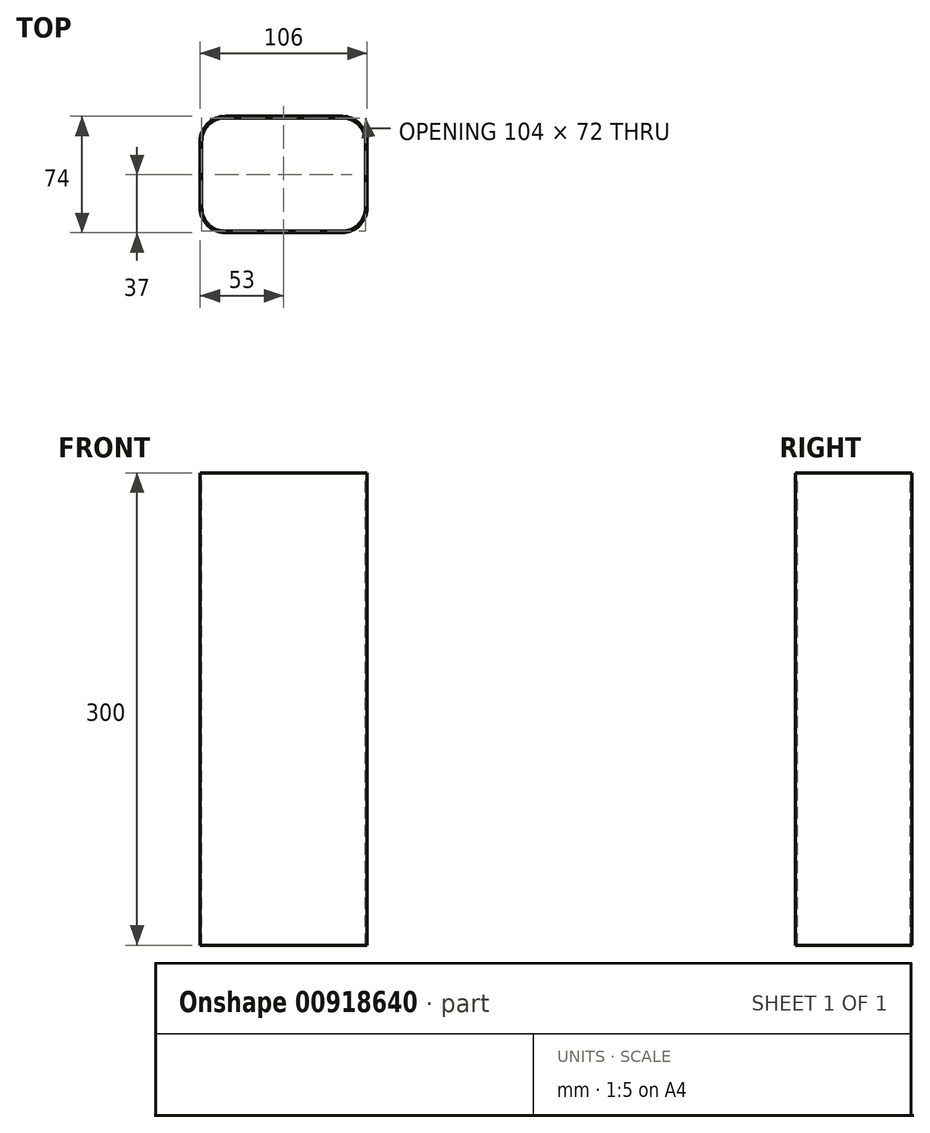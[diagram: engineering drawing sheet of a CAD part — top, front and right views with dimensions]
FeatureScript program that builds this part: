
annotation { "Feature Type Name" : "Feature", "Feature Type Description" : "" }
export const myFeature = defineFeature(function(context is Context, id is Id, definition is map)
    precondition{}
    {
        {
            var Q0;
            Q0=qCreatedBy(makeId("Top.planeOp"),FACE);
            var sketch = newSketch(context, id + "F0", { "sketchPlane" : qUnion([Q0])});
            skLineSegment(sketch, "E0.bottom", {"start": v(37, 37) * mm, "end": v(-37, 37) * mm});
            skLineSegment(sketch, "E0.top", {"start": v(37, -37) * mm, "end": v(-37, -37) * mm});
            skLineSegment(sketch, "E0.left", {"start": v(53, 21) * mm, "end": v(53, -21) * mm});
            skLineSegment(sketch, "E0.right", {"start": v(-53, 21) * mm, "end": v(-53, -21) * mm});
            skPoint(sketch, "E0.middle", {"position": v(0, 0) * mm});
            skPoint(sketch, "E1", {"position": v(37, 21) * mm});
            skArc(sketch, "E2", {"start": v(52, 21) * mm, "mid": v(47.6, 31.6) * mm, "end": v(37, 36) * mm});
            skArc(sketch, "E3", {"start": v(53, 21) * mm, "mid": v(48.31, 32.31) * mm, "end": v(37, 37) * mm});
            skLineSegment(sketch, "E4.trimOffspring", {"start": v(52, 21) * mm, "end": v(52, -21) * mm});
            skLineSegment(sketch, "E5.trimOffspring", {"start": v(37, 36) * mm, "end": v(-37, 36) * mm});
            skPoint(sketch, "E6.left.start.orphan", {"position": v(52, 36) * mm});
            skPoint(sketch, "E7.orphan", {"position": v(53, 37) * mm});
            skPoint(sketch, "E8", {"position": v(-37, -21) * mm});
            skArc(sketch, "E9", {"start": v(-52, -21) * mm, "mid": v(-47.6, -31.6) * mm, "end": v(-37, -36) * mm});
            skArc(sketch, "E10", {"start": v(-53, -21) * mm, "mid": v(-48.31, -32.31) * mm, "end": v(-37, -37) * mm});
            skPoint(sketch, "E11.orphan", {"position": v(-53, -37) * mm});
            skPoint(sketch, "E12.orphan", {"position": v(-52, -36) * mm});
            skPoint(sketch, "E13", {"position": v(-37, 21) * mm});
            skArc(sketch, "E14", {"start": v(-37, 36) * mm, "mid": v(-47.6, 31.6) * mm, "end": v(-52, 21) * mm});
            skArc(sketch, "E15", {"start": v(-37, 37) * mm, "mid": v(-48.31, 32.31) * mm, "end": v(-53, 21) * mm});
            skLineSegment(sketch, "E16.trimOffspring", {"start": v(-52, 21) * mm, "end": v(-52, -21) * mm});
            skPoint(sketch, "E17.orphan", {"position": v(-53, 37) * mm});
            skPoint(sketch, "E18.trimOffspring.end.orphan", {"position": v(-52, 36) * mm});
            skArc(sketch, "E19", {"start": v(37, -36) * mm, "mid": v(47.6, -31.6) * mm, "end": v(52, -21) * mm});
            skArc(sketch, "E20", {"start": v(37, -37) * mm, "mid": v(48.31, -32.31) * mm, "end": v(53, -21) * mm});
            skLineSegment(sketch, "E21.trimOffspring", {"start": v(37, -36) * mm, "end": v(-37, -36) * mm});
            skPoint(sketch, "E6.top.start.orphan", {"position": v(52, -36) * mm});
            skPoint(sketch, "E22.orphan", {"position": v(53, -37) * mm});
            skSolve(sketch);
        }
        {
            var Q0;
            Q0=qSketchRegion(id+"F0",true);
            extrude(context, id + "F1", {"entities" : qUnion([Q0]), "oppositeDirection" : true, "depth" : 300 * mm, "offsetDistance" : 25 * mm});
        }
    });
